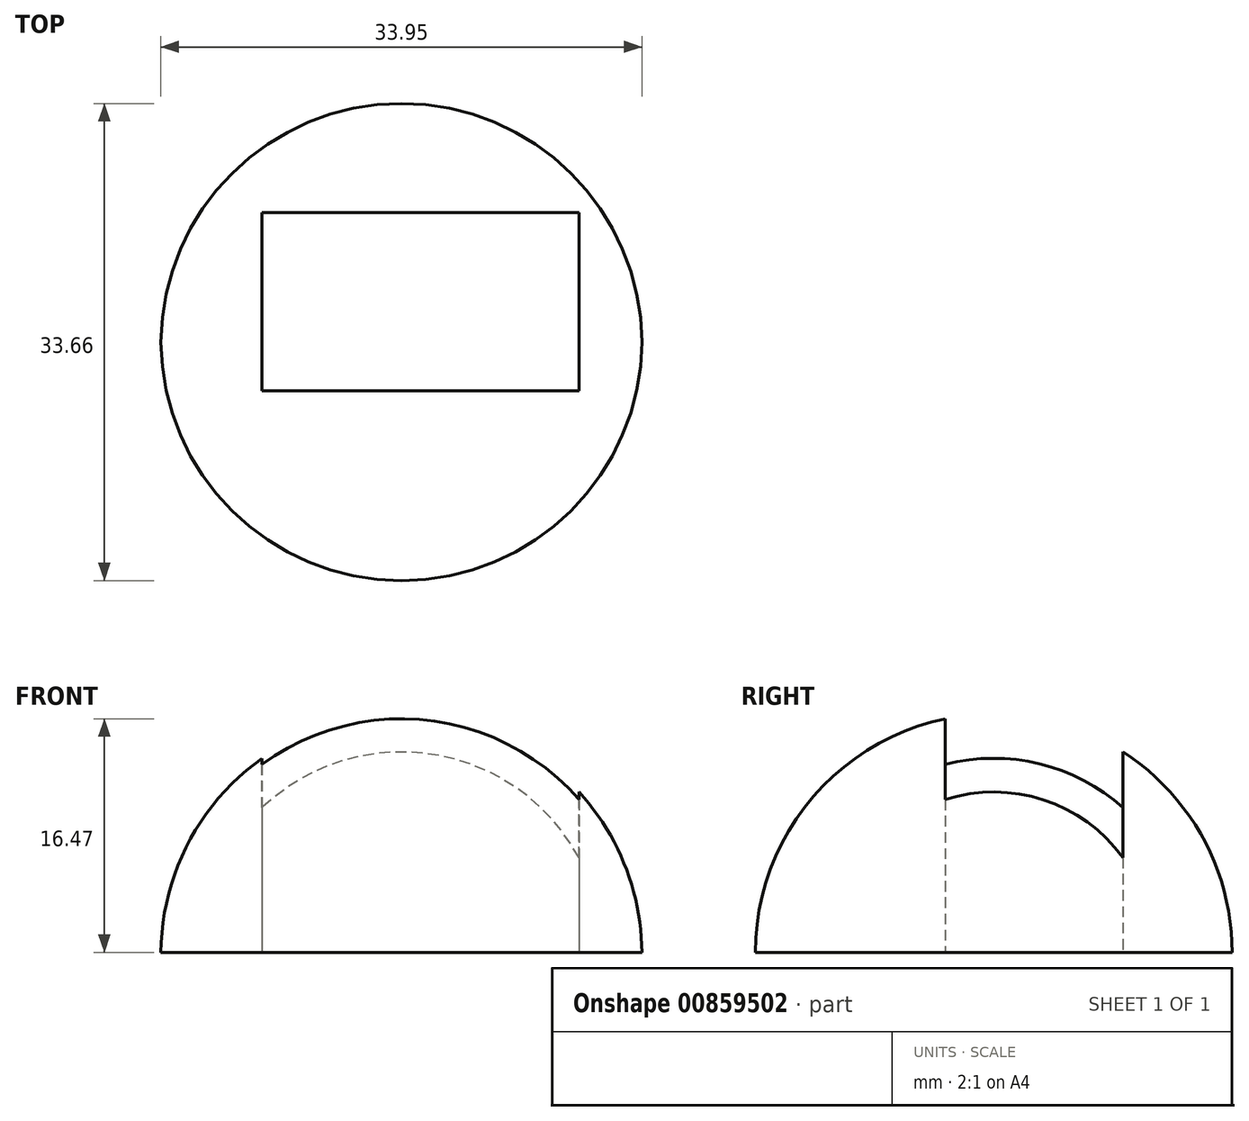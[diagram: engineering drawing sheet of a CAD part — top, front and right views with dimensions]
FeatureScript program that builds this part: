
annotation { "Feature Type Name" : "Feature", "Feature Type Description" : "" }
export const myFeature = defineFeature(function(context is Context, id is Id, definition is map)
    precondition{}
    {
        {
            var Q0;
            Q0=qCreatedBy(makeId("Top.planeOp"),FACE);
            var sketch = newSketch(context, id + "F0", { "sketchPlane" : qUnion([Q0])});
            skArc(sketch, "E0", {"start": v(-33.95, 0) * mm, "mid": v(-16.98, -16.83) * mm, "end": v(0, 0) * mm});
            skLineSegment(sketch, "E1", {"start": v(-33.95, 0) * mm, "end": v(0, 0) * mm});
            skSolve(sketch);
        }
        {
            var Q0;
            Q0=makeQuery(id+"F0.imprint","IMPRINT",FACE,{"disambiguationData":[TD([[makeQuery(id+"F0.imprint","IMPRINT",EDGE,{"derivedFrom":sQuery(id+"F0.wireOp",EDGE,"E0")}),1.0]])]});
            var Q1;
            Q1=sQuery(id+"F0.wireOp",EDGE,"E1");
            revolve(context, id + "F1", {"surfaceOperationType" : NewSurfaceOperationType.NEW, "entities" : qUnion([Q0]), "axis" : qUnion([Q1]), "revolveType" : RevolveType.FULL});
        }
        {
            var Q0;
            Q0=qCreatedBy(makeId("Top.planeOp"),FACE);
            var sketch = newSketch(context, id + "F2", { "sketchPlane" : qUnion([Q0])});
            skLineSegment(sketch, "E2.bottom", {"start": v(-46.6, -35.3) * mm, "end": v(10.23, -35.3) * mm});
            skLineSegment(sketch, "E2.top", {"start": v(-46.6, 45.69) * mm, "end": v(10.23, 45.69) * mm});
            skLineSegment(sketch, "E2.left", {"start": v(-46.6, -35.3) * mm, "end": v(-46.6, 45.69) * mm});
            skLineSegment(sketch, "E2.right", {"start": v(10.23, -35.3) * mm, "end": v(10.23, 45.69) * mm});
            skSolve(sketch);
        }
        {
            var Q0;
            Q0 = qSketchRegion(id + "F2", true);
            extrude(context, id + "F3", {"entities" : qUnion([Q0]), "operationType" : NewBodyOperationType.REMOVE, "oppositeDirection" : true, "depth" : 25.4 * mm, "offsetDistance" : 25.4 * mm});
        }
        {
            var Q0;
            Q0=qCreatedBy(makeId("Top.planeOp"),FACE);
            var sketch = newSketch(context, id + "F4", { "sketchPlane" : qUnion([Q0])});
            skLineSegment(sketch, "E3.bottom", {"start": v(-26.81, 9.12) * mm, "end": v(-4.45, 9.12) * mm});
            skLineSegment(sketch, "E3.top", {"start": v(-26.81, -3.43) * mm, "end": v(-4.45, -3.43) * mm});
            skLineSegment(sketch, "E3.left", {"start": v(-26.81, 9.12) * mm, "end": v(-26.81, -3.43) * mm});
            skLineSegment(sketch, "E3.right", {"start": v(-4.45, 9.12) * mm, "end": v(-4.45, -3.43) * mm});
            skSolve(sketch);
        }
        {
            var Q0;
            Q0=makeQuery(id+"F4.imprint","IMPRINT",FACE,{"disambiguationData":[TD([[makeQuery(id+"F4.imprint","IMPRINT",EDGE,{"derivedFrom":sQuery(id+"F4.wireOp",EDGE,"E3.bottom")}),-1.0]])]});
            extrude(context, id + "F5", {"entities" : qUnion([Q0]), "operationType" : NewBodyOperationType.REMOVE, "depth" : 25.4 * mm, "offsetDistance" : 25.4 * mm});
        }
    });
